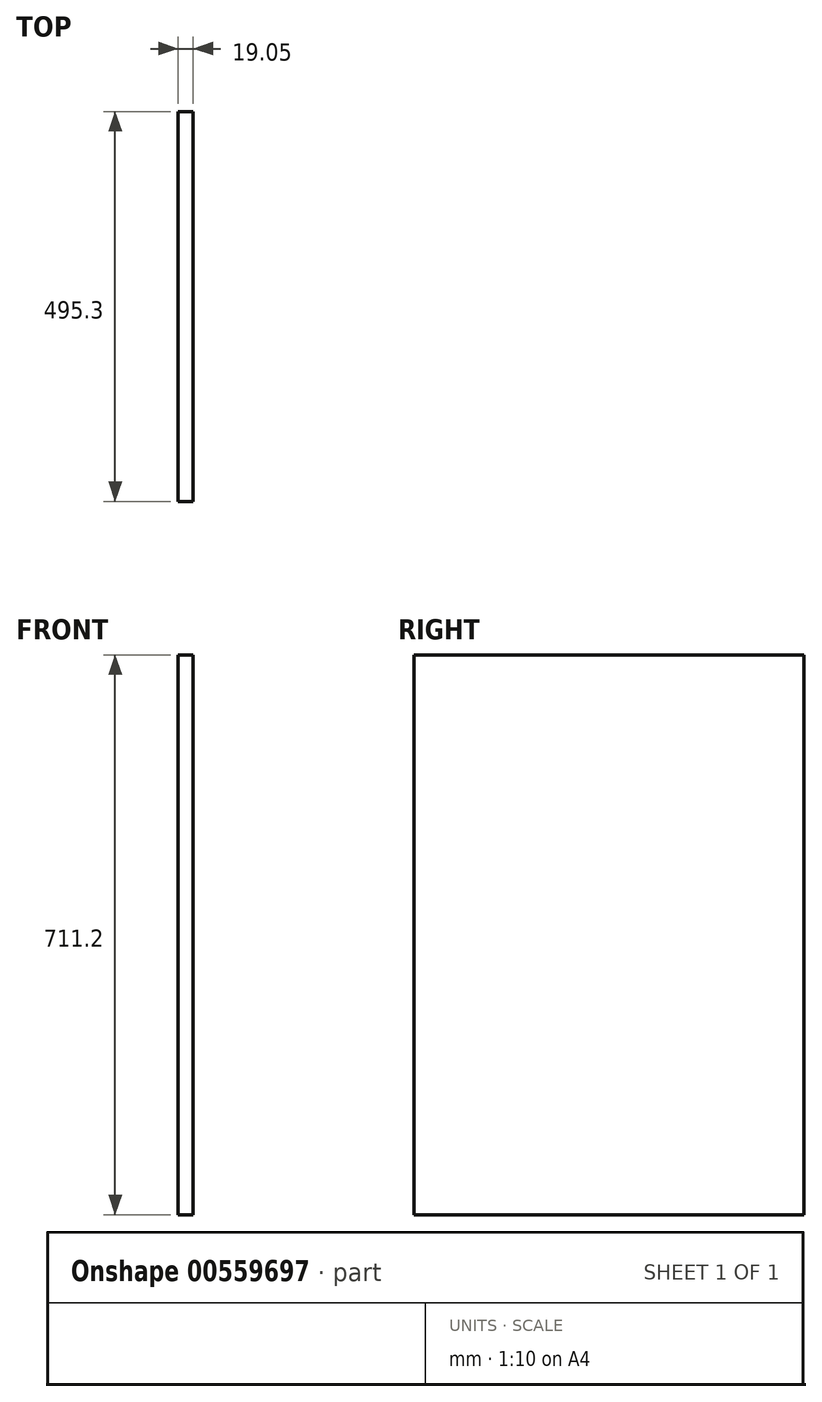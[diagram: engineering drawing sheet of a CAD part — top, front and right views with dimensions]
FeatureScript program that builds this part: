
annotation { "Feature Type Name" : "Feature", "Feature Type Description" : "" }
export const myFeature = defineFeature(function(context is Context, id is Id, definition is map)
    precondition{}
    {
        {
            var Q0;
            Q0=qCreatedBy(makeId("Right.planeOp"),FACE);
            var sketch = newSketch(context, id + "F0", { "sketchPlane" : qUnion([Q0])});
            skLineSegment(sketch, "E0.bottom", {"start": v(247.65, -355.6) * mm, "end": v(-247.65, -355.6) * mm});
            skLineSegment(sketch, "E0.top", {"start": v(247.65, 355.6) * mm, "end": v(-247.65, 355.6) * mm});
            skLineSegment(sketch, "E0.left", {"start": v(247.65, -355.6) * mm, "end": v(247.65, 355.6) * mm});
            skLineSegment(sketch, "E0.right", {"start": v(-247.65, -355.6) * mm, "end": v(-247.65, 355.6) * mm});
            skPoint(sketch, "E0.middle", {"position": v(0, 0) * mm});
            skSolve(sketch);
        }
        {
            var Q0;
            Q0 = qSketchRegion(id + "F0", true);
            extrude(context, id + "F1", {"entities" : qUnion([Q0]), "depth" : 19.05 * mm, "offsetDistance" : 25.4 * mm});
        }
    });
